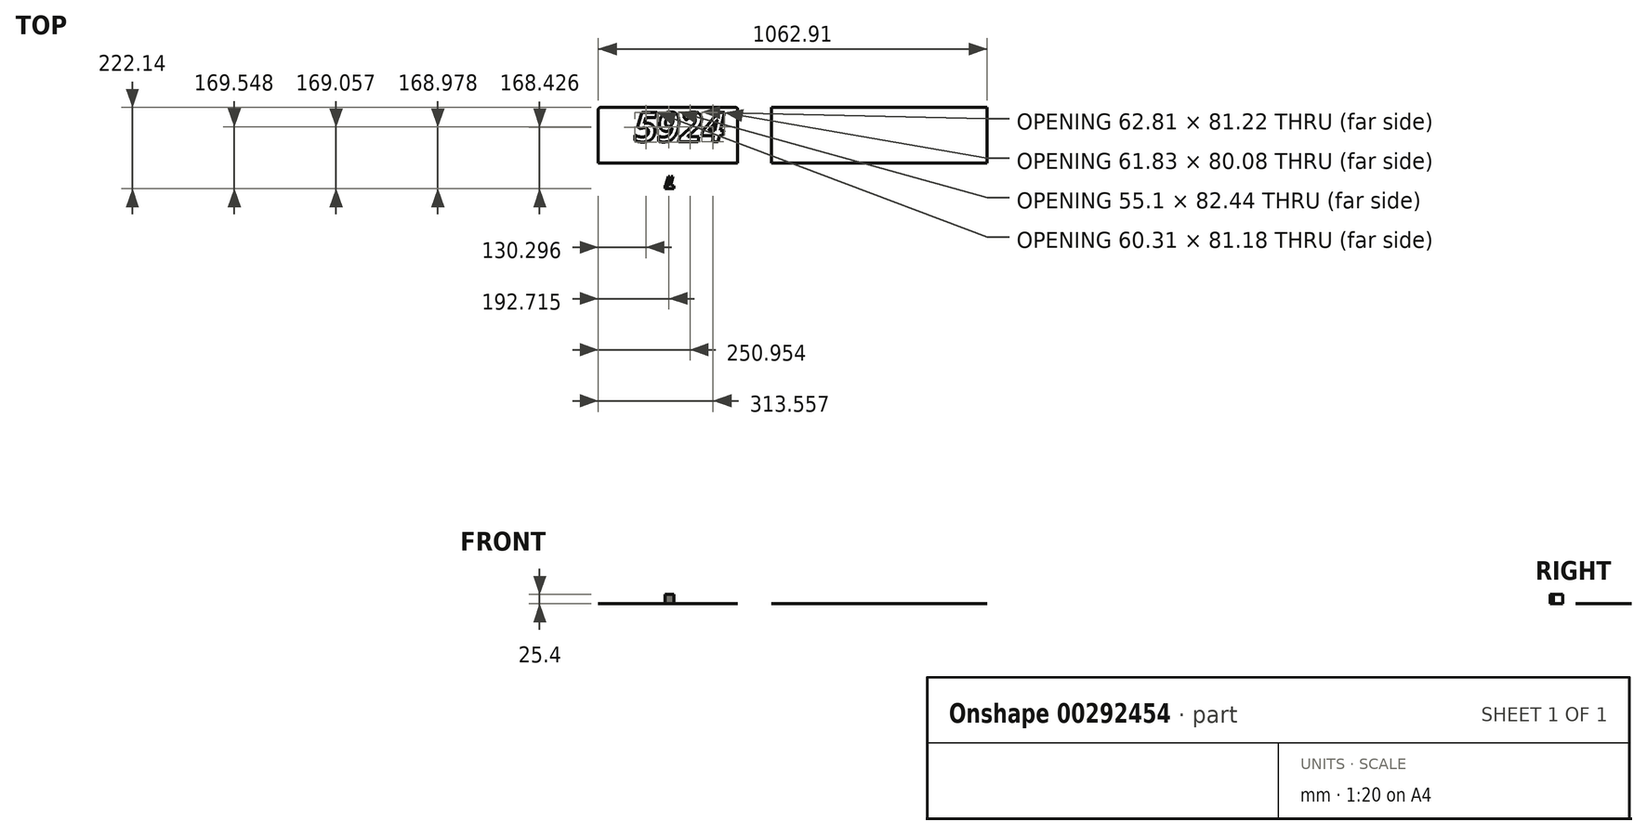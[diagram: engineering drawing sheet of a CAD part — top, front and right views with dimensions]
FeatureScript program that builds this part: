
annotation { "Feature Type Name" : "Feature", "Feature Type Description" : "" }
export const myFeature = defineFeature(function(context is Context, id is Id, definition is map)
    precondition{}
    {
        {
            var Q0;
            Q0=qCreatedBy(makeId("Top.planeOp"),FACE);
            var sketch = newSketch(context, id + "F0", { "sketchPlane" : qUnion([Q0])});
            skLineSegment(sketch, "E0.bottom", {"start": v(175.32, 6.25) * mm, "end": v(-205.68, 6.25) * mm});
            skLineSegment(sketch, "E0.top", {"start": v(175.32, 158.65) * mm, "end": v(-205.68, 158.65) * mm});
            skLineSegment(sketch, "E0.left", {"start": v(175.32, 6.25) * mm, "end": v(175.32, 158.65) * mm});
            skLineSegment(sketch, "E0.right", {"start": v(-205.68, 6.25) * mm, "end": v(-205.68, 158.65) * mm});
            skLineSegment(sketch, "E1.bottom", {"start": v(267.24, 158.65) * mm, "end": v(857.23, 158.65) * mm});
            skLineSegment(sketch, "E1.top", {"start": v(267.24, 6.25) * mm, "end": v(857.23, 6.25) * mm});
            skLineSegment(sketch, "E1.left", {"start": v(267.24, 158.65) * mm, "end": v(267.24, 6.25) * mm});
            skLineSegment(sketch, "E1.right", {"start": v(857.23, 158.65) * mm, "end": v(857.23, 6.25) * mm});
            skSolve(sketch);
        }
        {
            var Q0;
            Q0=makeQuery(id+"F0.imprint","IMPRINT",FACE,{"disambiguationData":[TD([[makeQuery(id+"F0.imprint","IMPRINT",EDGE,{"derivedFrom":sQuery(id+"F0.wireOp",EDGE,"E0.bottom")}),-1.0]])]});
            extrude(context, id + "F1", {"entities" : qUnion([Q0]), "depth" : 3 / 406.4 * mm});
        }
        {
            var Q0;
            Q0=makeQuery(id+"F1.opExtrude","CAP_FACE",FACE,{"disambiguationData":[OSD([sQuery(id+"F0.wireOp",EDGE,"E0.bottom"),sQuery(id+"F0.wireOp",EDGE,"E0.top"),sQuery(id+"F0.wireOp",EDGE,"E0.left"),sQuery(id+"F0.wireOp",EDGE,"E0.right")])],"isStart":false});
            var sketch = newSketch(context, id + "F2", { "sketchPlane" : qUnion([Q0])});
            skLineSegment(sketch, "E2.0", {"start": v(175.32, 158.65) * mm, "end": v(-205.68, 158.65) * mm});
            skLineSegment(sketch, "E3.0", {"start": v(-205.68, 6.25) * mm, "end": v(-205.68, 158.65) * mm});
            skLineSegment(sketch, "E4.bottom", {"start": v(146.06, 65.45) * mm, "end": v(-107.01, 65.45) * mm, "construction": true});
            skLineSegment(sketch, "E4.top", {"start": v(146.06, 146.21) * mm, "end": v(-107.01, 146.21) * mm, "construction": true});
            skLineSegment(sketch, "E4.left", {"start": v(146.06, 65.45) * mm, "end": v(146.06, 146.21) * mm, "construction": true});
            skLineSegment(sketch, "E4.right", {"start": v(-107.01, 65.45) * mm, "end": v(-107.01, 146.21) * mm, "construction": true});
            skText(sketch, "E5", { "text": "5924", "fontName": "OpenSans-BoldItalic.ttf"});
            const initialGuessF2  = {"E5": [-0.10701, 0.06545, 1, 0, 0.08076]};
            skSetInitialGuess(sketch, initialGuessF2);
            skSolve(sketch);
        }
        {
            var Q0;
            Q0 = qSketchRegion(id + "F2", true);
            extrude(context, id + "F3", {"entities" : qUnion([Q0]), "operationType" : NewBodyOperationType.REMOVE, "oppositeDirection" : true, "depth" : 2.5 * mm});
        }
        {
            var Q0;
            Q0=makeQuery(id+"F1.opExtrude","SWEPT_EDGE",EDGE,{"disambiguationData":[OSD([sQuery(id+"F0.wireOp",EDGE,"E0.top"),sQuery(id+"F0.wireOp",EDGE,"E0.right")])]});
            var Q1;
            Q1=makeQuery(id+"F1.opExtrude","SWEPT_EDGE",EDGE,{"disambiguationData":[OSD([sQuery(id+"F0.wireOp",EDGE,"E0.top"),sQuery(id+"F0.wireOp",EDGE,"E0.left")])]});
            fillet(context, id + "F4", {"entities" : qUnion([Q0, Q1]), "radius" : 5.08 * mm, "tangentPropagation" : true, "allowEdgeOverflow" : false});
        }
        {
            var Q0;
            Q0=makeQuery(id+"F0.imprint","IMPRINT",FACE,{"disambiguationData":[TD([[makeQuery(id+"F0.imprint","IMPRINT",EDGE,{"derivedFrom":sQuery(id+"F0.wireOp",EDGE,"E1.bottom")}),-1.0]])]});
            extrude(context, id + "F5", {"entities" : qUnion([Q0]), "depth" : 3 / 406.4 * mm});
        }
        {
            var Q0;
            Q0=qCreatedBy(makeId("Top.planeOp"),FACE);
            var sketch = newSketch(context, id + "F6", { "sketchPlane" : qUnion([Q0])});
            skLineSegment(sketch, "E6.bottom", {"start": v(-14.44, -29.56) * mm, "end": v(-11.16, -29.56) * mm});
            skLineSegment(sketch, "E6.top", {"start": v(-23.39, -63.5) * mm, "end": v(0.2, -63.5) * mm});
            skLineSegment(sketch, "E6.left", {"start": v(-23.39, -54.96) * mm, "end": v(-23.39, -63.5) * mm});
            skLineSegment(sketch, "E6.right", {"start": v(0.2, -54.96) * mm, "end": v(0.2, -63.5) * mm});
            skLineSegment(sketch, "E7", {"start": v(-17.97, -54.96) * mm, "end": v(-11.16, -29.56) * mm});
            skLineSegment(sketch, "E8", {"start": v(-6.4, -29.56) * mm, "end": v(-13.2, -54.96) * mm});
            skLineSegment(sketch, "E9", {"start": v(-17.97, -54.96) * mm, "end": v(-13.2, -54.96) * mm});
            skLineSegment(sketch, "E10", {"start": v(-14.44, -29.56) * mm, "end": v(-21.24, -54.96) * mm});
            skLineSegment(sketch, "E11", {"start": v(-1.1, -29.56) * mm, "end": v(-7.91, -54.96) * mm});
            skLineSegment(sketch, "E12.trimOffspring", {"start": v(-6.4, -29.56) * mm, "end": v(-1.1, -29.56) * mm});
            skPoint(sketch, "E13.orphan", {"position": v(0.2, -29.56) * mm});
            skLineSegment(sketch, "E14", {"start": v(-21.24, -54.96) * mm, "end": v(-23.39, -54.96) * mm});
            skLineSegment(sketch, "E15", {"start": v(-7.91, -54.96) * mm, "end": v(0.2, -54.96) * mm});
            skSolve(sketch);
        }
        {
            var Q0;
            Q0=makeQuery(id+"F6.imprint","IMPRINT",FACE,{"disambiguationData":[TD([[makeQuery(id+"F6.imprint","IMPRINT",EDGE,{"derivedFrom":sQuery(id+"F6.wireOp",EDGE,"E6.top")}),1.0]])]});
            extrude(context, id + "F7", {"entities" : qUnion([Q0]), "depth" : 25.4 * mm});
        }
        {
            var Q0;
            Q0=makeQuery(id+"F7.opExtrude","SWEPT_EDGE",EDGE,{"disambiguationData":[OSD([sQuery(id+"F6.wireOp",EDGE,"E11"),sQuery(id+"F6.wireOp",EDGE,"E15")])]});
            var Q1;
            Q1=makeQuery(id+"F7.opExtrude","SWEPT_EDGE",EDGE,{"disambiguationData":[OSD([sQuery(id+"F6.wireOp",EDGE,"E10"),sQuery(id+"F6.wireOp",EDGE,"E14")])]});
            fillet(context, id + "F8", {"entities" : qUnion([Q0, Q1]), "radius" : 5.08 * mm, "tangentPropagation" : true, "allowEdgeOverflow" : false});
        }
    });
